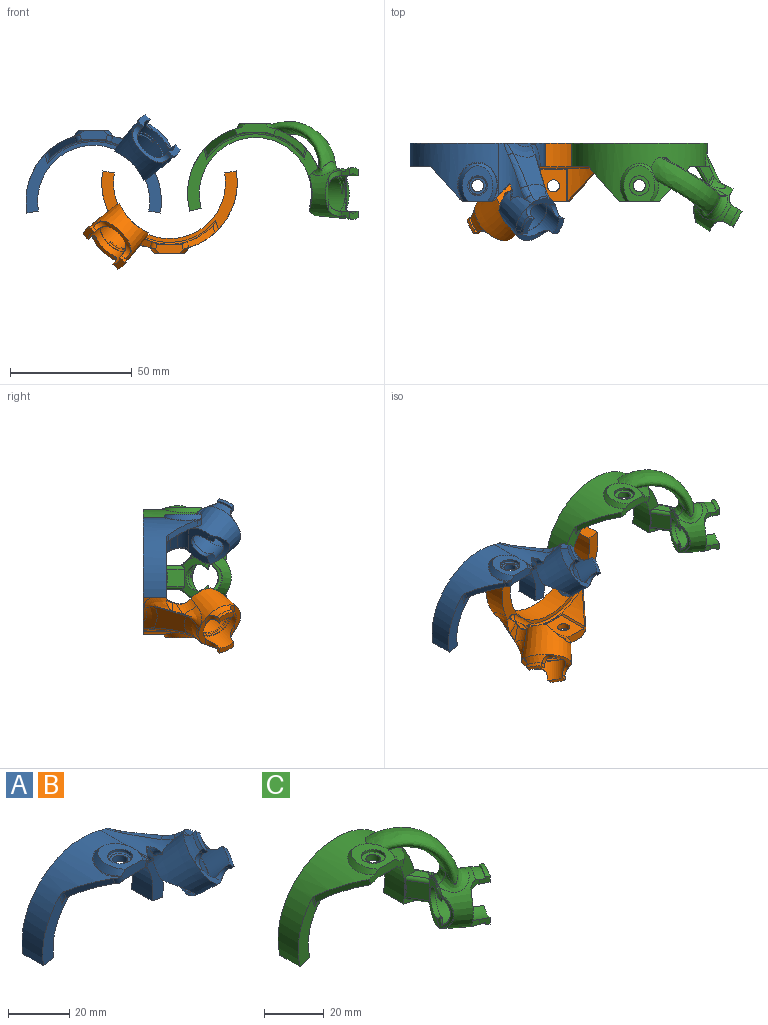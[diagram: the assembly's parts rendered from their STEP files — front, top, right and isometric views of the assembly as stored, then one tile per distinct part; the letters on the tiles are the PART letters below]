
ASSEMBLY  parts=3 mates=2
PART A: 82 faces, bbox 63.7x43.6x40.7 mm
  f0: cylinder r=27.82mm len=27.72mm, axis (0,-1,0), area 190.1mm2, adj f8,f10,f11,f62,f64
  f1: plane 11.92x10.64mm, normal (0.68,-0.71,-0.2), area 38.9mm2, adj f4,f5,f7,f27,f75,f76
  f2: cylinder r=2.48mm len=4.95mm, axis (0,0,-1), area 37.8mm2, adj f6,f21
  f3: cylinder r=2.54mm len=3.26mm, axis (-0.28,0,0.96), area 7.4mm2, adj f5,f7,f13,f14,f19,f21,f23,f25
  f4: cylinder r=2.54mm len=3.26mm, axis (-0.28,0,-0.96), area 7.4mm2, adj f1,f5,f7,f13,f19,f21,f24,f25
  f5: cylinder r=27.82mm len=36.56mm, axis (0,-1,0), area 638.5mm2, adj f1,f3,f4,f8,f10,f12,f14,f16
  f6: cylinder r=27.82mm len=7.09mm, axis (0,-1,0), area 19.5mm2, adj f2,f61
  f7: cylinder r=25.28mm len=35.25mm, axis (0,-1,0), area 190.1mm2, adj f1,f3,f4,f14,f15,f20,f22,f23
  f8: plane 55.71x29.42mm, normal (0,-1,0), area 248.8mm2, adj f0,f5,f9,f11,f12,f15,f16,f62
  f9: cylinder r=22.99mm len=45.98mm, axis (0,-1,0), area 764.4mm2, adj f8,f10,f11,f12
  f10: plane 56.02x33.04mm, normal (0,1,0), area 429.4mm2, adj f0,f5,f9,f11,f12,f63,f64,f77
  f11: plane 9.53x4.75mm, normal (-0.17,0,-0.98), area 46mm2, adj f0,f8,f9,f10
  f12: plane 9.53x4.75mm, normal (0.17,0,-0.98), area 46mm2, adj f5,f8,f9,f10
  f13: plane 11.35x3.84mm, normal (0,-1,0), area 39.1mm2, adj f3,f4,f18,f19,f21
  f14: plane 12.34x11.8mm, normal (-0.68,-0.71,-0.2), area 44.6mm2, adj f3,f5,f7,f15,f16
  f15: torus R=24.52mm, axis (0,-1,0), area 40.5mm2, adj f7,f8,f14,f16,f75
  f16: cylinder r=2.54mm len=5.13mm, axis (-0.28,0,0.96), area 6.7mm2, adj f5,f8,f14,f15
  f17: cylinder r=4.05mm len=8.1mm, axis (0,0,-1), area 24.8mm2, adj f18,f61
  f18: plane 14.63x12.64mm, normal (0,0,1), area 98.7mm2, adj f13,f17,f19
  f19: bspline ~16.86x15.94mm, area 92.9mm2, adj f3,f4,f13,f18,f25
  f20: plane 5.8x0.67mm, normal (0,-1,0), area 1.1mm2, adj f7,f21,f24
  f21: plane 12.98x10.54mm, normal (0,0,-1), area 117.5mm2, adj f2,f3,f4,f13,f20,f22,f23,f24
  f22: plane 5.8x0.67mm, normal (0,-1,0), area 1.1mm2, adj f7,f21,f23
  f23: plane 12.99x0.68mm, normal (0.78,0,-0.62), area 11.1mm2, adj f3,f7,f21,f22
  f24: plane 12.99x0.68mm, normal (-0.78,0,-0.62), area 11.1mm2, adj f4,f7,f20,f21
  f25: bspline ~17.23x16.47mm, area 14.5mm2, adj f3,f4,f5,f19
  f26: plane 4.77x4.77mm, normal (0.71,0,-0.71), area 13.3mm2, adj f55,f67,f70,f72
  f27: plane 11.43x9.08mm, normal (-0.65,-0.39,-0.65), area 33.3mm2, adj f1,f53,f56,f68,f69,f75
  f28: cone r=10.34mm half-angle=4.9deg, axis (0.59,-0.54,0.59), area 530.4mm2, adj f29,f30,f42,f43,f49,f52,f57,f58
  f29: cone r=10.34mm half-angle=8.1deg, axis (-0.59,0.54,-0.59), area 31.7mm2, adj f28,f32,f48,f51,f57,f58
  f30: cone r=10.34mm half-angle=8.1deg, axis (-0.59,0.54,-0.59), area 31.7mm2, adj f28,f31,f47,f50,f59,f60
  f31: plane 6.06x3.44mm, normal (-0.59,0.54,-0.59), area 6.6mm2, adj f30,f33,f47,f50
  f32: plane 6.06x3.44mm, normal (-0.59,0.54,-0.59), area 6.6mm2, adj f29,f34,f48,f51
  f33: cylinder r=10.72mm len=6.82mm, axis (-0.59,0.54,-0.59), area 10.3mm2, adj f31,f35,f47,f50
  f34: cylinder r=10.72mm len=6.82mm, axis (-0.59,0.54,-0.59), area 10.3mm2, adj f32,f36,f48,f51
  f35: plane 6.06x4.81mm, normal (0.59,-0.54,0.59), area 19.8mm2, adj f33,f37,f47,f50
  f36: plane 6.06x4.81mm, normal (0.59,-0.54,0.59), area 19.8mm2, adj f34,f37,f48,f51
  f37: cylinder r=8.05mm len=18.01mm, axis (-0.59,0.54,-0.59), area 249.8mm2, adj f35,f36,f40,f47,f48,f49,f50,f51
  f38: cylinder r=7.67mm len=17.35mm, axis (-0.59,0.54,-0.59), area 360.5mm2, adj f40,f41,f43,f44,f45,f46
  f39: cylinder r=5.29mm len=9.57mm, axis (-0.59,0.54,-0.59), area 42.1mm2, adj f41,f42,f43
  f40: plane 13.53x12.95mm, normal (0.59,-0.54,0.59), area 18.8mm2, adj f37,f38
  f41: plane 12.45x12.45mm, normal (0.59,-0.54,0.59), area 73.4mm2, adj f38,f39,f43
  f42: plane 15x15mm, normal (-0.59,0.54,-0.59), area 89mm2, adj f28,f39,f43,f67,f68,f69,f70
  f43: cylinder r=22.23mm len=11.7mm, axis (0,1,0), area 58.8mm2, adj f28,f38,f39,f41,f42
  f44: torus R=7.67mm, axis (-0.59,0.54,-0.59), area 23.4mm2, adj f38,f45,f46
  f45: plane 0.49x0.41mm, normal (0.71,0,-0.71), area 0.2mm2, adj f38,f44
  f46: plane 0.49x0.41mm, normal (0.71,0,-0.71), area 0.2mm2, adj f38,f44
  f47: plane 2.95x2.88mm, normal (-0.38,-0.84,-0.38), area 4.3mm2, adj f30,f31,f33,f35,f37,f59
  f48: plane 2.95x2.88mm, normal (-0.38,-0.84,-0.38), area 4.3mm2, adj f29,f32,f34,f36,f37,f58
  f49: plane 10.52x10.52mm, normal (0.59,-0.54,0.59), area 28.1mm2, adj f28,f37,f58,f59
  f50: plane 2.95x2.88mm, normal (0.38,0.84,0.38), area 4.3mm2, adj f30,f31,f33,f35,f37,f60
  f51: plane 2.95x2.88mm, normal (0.38,0.84,0.38), area 4.3mm2, adj f29,f32,f34,f36,f37,f57
  f52: plane 10.65x10.65mm, normal (0.59,-0.54,0.59), area 28.4mm2, adj f28,f37,f57,f60,f65,f81
  f53: plane 2.25x1.64mm, normal (-0.68,-0.28,-0.68), area 2.3mm2, adj f27,f63,f68,f76
  f54: plane 13.87x13.1mm, normal (0.65,0.39,0.65), area 138.7mm2, adj f55,f64,f65,f78
  f55: cylinder r=0.25mm len=15.15mm, axis (-0.27,0.92,-0.27), area 4.6mm2, adj f26,f54,f62,f66,f71
  f56: cylinder r=0.25mm len=3.04mm, axis (0.27,-0.92,0.27), area 0.6mm2, adj f27,f70,f74
  f57: cylinder r=3.56mm len=5.03mm, axis (0.71,0,-0.71), area 13.1mm2, adj f28,f29,f37,f51,f52
  f58: cylinder r=3.56mm len=7.36mm, axis (-0.71,0,0.71), area 13.1mm2, adj f28,f29,f37,f48,f49
  f59: cylinder r=3.56mm len=7.36mm, axis (-0.71,0,0.71), area 13.1mm2, adj f28,f30,f37,f47,f49
  f60: cylinder r=3.56mm len=5.03mm, axis (0.71,0,-0.71), area 13.1mm2, adj f28,f30,f37,f50,f52
  f61: bspline ~8.12x8.11mm, area 20.1mm2, adj f6,f17
  f62: bspline ~12.74x8.36mm, area 48.6mm2, adj f0,f8,f55,f64,f71,f72
  f63: cylinder r=10.92mm len=23.59mm, axis (0,-1,0), area 126.5mm2, adj f5,f10,f28,f53,f68,f76,f77,f78
  f64: bspline ~12.26x10.49mm, area 58.9mm2, adj f0,f10,f54,f62,f77
  f65: bspline ~11.42x11.17mm, area 64.6mm2, adj f28,f52,f54,f66,f79,f80,f81
  f66: bspline ~11.15x9.59mm, area 43.5mm2, adj f28,f55,f65,f67
  f67: bspline ~18.46x16.46mm, area 37mm2, adj f26,f28,f42,f66,f70
  f68: bspline ~12.69x12.02mm, area 17mm2, adj f27,f28,f42,f53,f63,f69
  f69: cylinder r=5.08mm len=8.78mm, axis (0.71,0,-0.71), area 48.6mm2, adj f27,f42,f68,f70
  f70: bspline ~7.07x5.36mm, area 3.7mm2, adj f26,f42,f56,f67,f69,f72,f73
  f71: bspline ~3.08x3.03mm, area 0mm2, adj f55,f62,f72
  f72: cylinder r=2.54mm len=5.65mm, axis (-0.71,0,-0.71), area 13.5mm2, adj f8,f26,f62,f70,f71,f73
  f73: bspline ~3.31x2.86mm, area 0.9mm2, adj f8,f70,f72,f74
  f74: bspline ~3.3x2.58mm, area 5.8mm2, adj f8,f56,f73,f75
  f75: cylinder r=2.54mm len=10.94mm, axis (-0.71,0,0.71), area 28.7mm2, adj f1,f7,f8,f15,f27,f74
  f76: bspline ~7.88x7.71mm, area 1.7mm2, adj f1,f5,f53,f63
  f77: bspline ~8.1x4.83mm, area 9.2mm2, adj f10,f63,f64,f78
  f78: bspline ~14.69x8.01mm, area 43.3mm2, adj f54,f63,f77,f79
  f79: bspline ~7.97x5.64mm, area 15.7mm2, adj f63,f65,f78,f80
  f80: bspline ~3.64x2.8mm, area 0.7mm2, adj f28,f65,f79,f81
  f81: bspline ~4.33x3.86mm, area 9.3mm2, adj f28,f52,f65,f80
PART B: same geometry as A
PART C: 123 faces, bbox 86.5x40.3x50.3 mm
  f0: cylinder r=7.8mm len=17.92mm, axis (-0.88,0.48,0), area 376mm2, adj f35,f47,f48,f49,f80,f81,f82,f91
  f1: plane 16.83x4.8mm, normal (0,-1,0), area 49.3mm2, adj f17,f19,f25,f26,f31,f32,f86,f87
  f2: cylinder r=2.48mm len=4.95mm, axis (0,0,-1), area 37.8mm2, adj f18,f86
  f3: cone r=10.21mm half-angle=4.9deg, axis (0.88,-0.48,0), area 394.1mm2, adj f6,f7,f9,f10,f41,f44,f50,f51
  f4: cylinder r=5.42mm len=10.83mm, axis (-0.88,0.48,0), area 45.1mm2, adj f36,f76,f79,f80,f82,f83,f91,f92
  f5: plane 8.22x7.83mm, normal (-0.86,-0.51,0), area 57.7mm2, adj f20,f36,f59,f61,f77
  f6: cone r=8.31mm half-angle=47.5deg, axis (0.88,-0.48,0), area 14.2mm2, adj f3,f36,f70,f76,f83,f84
  f7: cone r=8.31mm half-angle=47.5deg, axis (0.88,-0.48,0), area 2.5mm2, adj f3,f36,f71,f76,f78,f84
  f8: cylinder r=8.18mm len=18.31mm, axis (-0.88,0.48,0), area 166.1mm2, adj f15,f16,f35,f41,f42,f43,f44,f45
  f9: cone r=10.21mm half-angle=8.4deg, axis (-0.88,0.48,0), area 26.7mm2, adj f3,f12,f43,f46,f50,f51
  f10: cone r=10.21mm half-angle=8.4deg, axis (-0.88,0.48,0), area 26.7mm2, adj f3,f11,f42,f45,f52,f53
  f11: plane 6.54x3.61mm, normal (-0.88,0.48,0), area 6.8mm2, adj f10,f13,f42,f45
  f12: plane 6.54x3.61mm, normal (-0.88,0.48,0), area 6.8mm2, adj f9,f14,f43,f46
  f13: cylinder r=10.59mm len=7.3mm, axis (-0.88,0.48,0), area 12.1mm2, adj f11,f15,f42,f45
  f14: cylinder r=10.59mm len=7.3mm, axis (-0.88,0.48,0), area 12.1mm2, adj f12,f16,f43,f46
  f15: plane 6.54x3.61mm, normal (0.88,-0.48,0), area 18.5mm2, adj f8,f13,f42,f45
  f16: plane 6.54x3.61mm, normal (0.88,-0.48,0), area 18.5mm2, adj f8,f14,f43,f46
  f17: cylinder r=27.82mm len=55.64mm, axis (0,-1,0), area 1084.1mm2, adj f1,f20,f22,f23,f24,f25,f26,f28
  f18: cylinder r=27.82mm len=8.1mm, axis (0,-1,0), area 32.4mm2, adj f2,f30
  f19: cylinder r=25.28mm len=38.76mm, axis (0,-1,0), area 257.7mm2, adj f1,f25,f26,f27,f40,f85,f87,f88
  f20: plane 56.83x31.78mm, normal (0,-1,0), area 251.4mm2, adj f5,f17,f21,f23,f24,f27,f28,f29
  f21: cylinder r=22.99mm len=45.98mm, axis (0,-1,0), area 802.7mm2, adj f20,f22,f23,f24
  f22: plane 55.64x35.02mm, normal (0,1,0), area 449.4mm2, adj f17,f21,f23,f24
  f23: plane 9.53x4.66mm, normal (-0.26,0,-0.97), area 46mm2, adj f17,f20,f21,f22
  f24: plane 9.53x4.66mm, normal (0.26,0,-0.97), area 46mm2, adj f17,f20,f21,f22
  f25: plane 14.01x13.01mm, normal (0.68,-0.71,-0.2), area 53.3mm2, adj f1,f17,f19,f27,f28
  f26: plane 14.01x13.01mm, normal (-0.68,-0.71,-0.2), area 53.3mm2, adj f1,f17,f19,f27,f29
  f27: torus R=24.52mm, axis (0,-1,0), area 53.6mm2, adj f19,f20,f25,f26,f28,f29,f40,f90
  f28: cylinder r=1.02mm len=4.53mm, axis (0.28,0,0.96), area 2.9mm2, adj f17,f20,f25,f27
  f29: cylinder r=1.02mm len=4.53mm, axis (-0.28,0,0.96), area 2.9mm2, adj f17,f20,f26,f27
  f30: cylinder r=4.05mm len=8.1mm, axis (0,0,-1), area 30.2mm2, adj f18,f31
  f31: plane 16.69x14.85mm, normal (0,0,1), area 102.5mm2, adj f1,f30,f32
  f32: bspline ~16.48x15.78mm, area 58.7mm2, adj f1,f17,f31,f38
  f33: plane 6.25x6.23mm, normal (0,0,-1), area 19.8mm2, adj f20,f60,f61,f66,f70
  f34: plane 6.25x6.23mm, normal (0,0,1), area 19.8mm2, adj f20,f58,f59,f62,f75
  f35: plane 16.36x14.32mm, normal (0.88,-0.48,0), area 19.1mm2, adj f0,f8
  f36: plane 17.15x10.58mm, normal (-0.88,0.48,0), area 71.8mm2, adj f4,f5,f6,f7,f59,f61,f70,f71
  f37: plane 10.24x6.99mm, normal (0.9,0.43,0), area 74.1mm2, adj f58,f60,f64,f68
  f38: bspline ~33.42x32.82mm, area 654.6mm2, adj f17,f32,f54,f56,f94,f98
  f39: plane 22.53x17.34mm, normal (0.48,0.87,-0.14), area 75.6mm2, adj f57,f94,f95,f96,f98,f99,f101
  f40: bspline ~28.97x28.69mm, area 0.2mm2, adj f19,f27,f90
  f41: plane 13.09x2.14mm, normal (0.88,-0.48,0), area 19.2mm2, adj f3,f8,f51,f52
  f42: plane 3.34x2.64mm, normal (-0.48,-0.88,0), area 8.3mm2, adj f8,f10,f11,f13,f15,f52
  f43: plane 3.34x2.64mm, normal (-0.48,-0.88,0), area 8.3mm2, adj f8,f9,f12,f14,f16,f51
  f44: plane 13.09x2.14mm, normal (0.88,-0.48,0), area 19.2mm2, adj f3,f8,f50,f53
  f45: plane 3.34x2.64mm, normal (0.48,0.88,0), area 8.3mm2, adj f8,f10,f11,f13,f15,f53
  f46: plane 3.34x2.64mm, normal (0.48,0.88,0), area 8.3mm2, adj f8,f9,f12,f14,f16,f50
  f47: torus R=7.8mm, axis (-0.88,0.48,0), area 25.7mm2, adj f0,f48,f49
  f48: plane 0.64x0.51mm, normal (0,0,-1), area 0.2mm2, adj f0,f47
  f49: plane 0.64x0.51mm, normal (0,0,-1), area 0.2mm2, adj f0,f47
  f50: cylinder r=3.81mm len=6.26mm, axis (0,0,-1), area 12.6mm2, adj f3,f8,f9,f44,f46
  f51: cylinder r=3.81mm len=6.26mm, axis (0,0,1), area 12.6mm2, adj f3,f8,f9,f41,f43
  f52: cylinder r=3.81mm len=6.26mm, axis (0,0,1), area 12.6mm2, adj f3,f8,f10,f41,f42
  f53: cylinder r=3.81mm len=6.26mm, axis (0,0,-1), area 12.6mm2, adj f3,f8,f10,f44,f45
  f54: bspline ~7.44x6.47mm, area 34.7mm2, adj f38,f55,f56,f72,f95
  f55: bspline ~7.43x6.95mm, area 7.8mm2, adj f3,f54,f73,f96,f97
  f56: bspline ~13.81x13.06mm, area 87.8mm2, adj f3,f38,f54,f71,f99,f100
  f57: bspline ~38.57x21.21mm, area 21.3mm2, adj f3,f39,f97,f100
  f58: cylinder r=1.27mm len=11.61mm, axis (0.43,-0.9,0), area 19.4mm2, adj f20,f34,f37,f63,f67
  f59: cylinder r=1.27mm len=8.02mm, axis (-0.51,0.86,0), area 15.9mm2, adj f5,f20,f34,f36,f75
  f60: cylinder r=1.27mm len=11.61mm, axis (-0.43,0.9,0), area 19.4mm2, adj f20,f33,f37,f65,f69
  f61: cylinder r=1.27mm len=8.02mm, axis (0.51,-0.86,0), area 15.9mm2, adj f5,f20,f33,f36,f70
  f62: bspline ~22.47x12.27mm, area 3.9mm2, adj f3,f34,f63,f75
  f63: bspline ~7.53x5.56mm, area 20.4mm2, adj f3,f58,f62,f64
  f64: bspline ~6.99x2.91mm, area 21.5mm2, adj f3,f37,f63,f65
  f65: bspline ~6.49x5.05mm, area 20.4mm2, adj f3,f60,f64,f66
  f66: bspline ~35.46x17.86mm, area 3.9mm2, adj f3,f33,f65,f70
  f67: bspline ~6.82x3.97mm, area 11.6mm2, adj f17,f20,f58,f68
  f68: bspline ~6.99x1.52mm, area 7.7mm2, adj f17,f37,f67,f69
  f69: bspline ~6.7x3.58mm, area 11.6mm2, adj f17,f20,f60,f68
  f70: bspline ~3.98x2.92mm, area 2.8mm2, adj f6,f33,f36,f61,f66
  f71: bspline ~1.71x1.24mm, area 1.4mm2, adj f7,f36,f56,f72
  f72: bspline ~5.42x3.41mm, area 5.3mm2, adj f36,f54,f71,f73
  f73: bspline ~1.41x1.39mm, area 1.3mm2, adj f36,f55,f72,f74
  f74: cone r=8.31mm half-angle=47.5deg, axis (0.88,-0.48,0), area 2.1mm2, adj f3,f36,f73,f75
  f75: bspline ~3.98x2.91mm, area 2.8mm2, adj f34,f36,f59,f62,f74
  f76: cylinder r=23.24mm len=13.92mm, axis (0,1,0), area 26.7mm2, adj f4,f6,f7,f78,f79,f80,f81,f82
  f77: cylinder r=23.24mm len=6.79mm, axis (0,1,0), area 0mm2, adj f5,f20
  f78: bspline ~2.53x1.27mm, area 0.4mm2, adj f7,f36,f76,f79
  f79: bspline ~3.94x2.76mm, area 0.9mm2, adj f4,f36,f76,f78,f80
  f80: bspline ~2.83x1.25mm, area 1.7mm2, adj f0,f4,f76,f79,f81,f93
  f81: bspline ~12.52x4.28mm, area 6.9mm2, adj f0,f76,f80,f82
  f82: bspline ~2.87x1.26mm, area 1.8mm2, adj f0,f4,f76,f81,f92
  f83: bspline ~2.7x1.33mm, area 0.4mm2, adj f4,f6,f36,f76
  f84: bspline ~15.01x5.63mm, area 5.4mm2, adj f3,f6,f7,f76
  f85: plane 5.08x0.52mm, normal (0,-1,0), area 0.9mm2, adj f19,f86,f88
  f86: plane 13.28x10.16mm, normal (0,0,-1), area 115.7mm2, adj f1,f2,f85,f87,f88,f89
  f87: plane 13.28x0.52mm, normal (1,0,0), area 6.9mm2, adj f1,f19,f86,f89
  f88: plane 13.28x0.52mm, normal (-1,0,0), area 6.9mm2, adj f1,f19,f85,f86
  f89: plane 5.08x0.52mm, normal (0,-1,0), area 0.9mm2, adj f19,f86,f87
  f90: bspline ~4.75x3.92mm, area 4.4mm2, adj f19,f27,f40
  f91: plane 15.6x9.75mm, normal (0.88,-0.48,0), area 63.3mm2, adj f0,f4,f92,f93
  f92: bspline ~3.62x2.56mm, area 5.7mm2, adj f0,f4,f82,f91
  f93: bspline ~3.62x2.56mm, area 5.7mm2, adj f0,f4,f80,f91
  f94: bspline ~20.39x13.51mm, area 24.5mm2, adj f17,f38,f39,f95,f101
  f95: bspline ~0.93x0.28mm, area 0.1mm2, adj f39,f54,f94,f96
  f96: bspline ~2.23x1.03mm, area 1.7mm2, adj f39,f55,f95,f97
  f97: bspline ~3.8x2.12mm, area 1.2mm2, adj f55,f57,f96
  f98: bspline ~26.24x17.22mm, area 34.1mm2, adj f17,f38,f39,f99,f101
  f99: bspline ~1.12x0.94mm, area 0.7mm2, adj f39,f56,f98,f100
  f100: bspline ~3.51x3.41mm, area 1.5mm2, adj f56,f57,f99
  f101: bspline ~3.41x2.76mm, area 3mm2, adj f17,f39,f94,f98
  f102: plane 2.23x1.23mm, normal (-0.26,0,0.97), area 2.8mm2, adj f103,f104,f105,f106
  f103: cylinder r=26.04mm len=52.08mm, axis (0,-1,0), area 207.4mm2, adj f102,f104,f106,f107
  f104: plane 52.08x31.55mm, normal (0,1,0), area 115mm2, adj f102,f103,f105,f107
  f105: cylinder r=24.77mm len=49.54mm, axis (0,-1,0), area 197mm2, adj f102,f104,f106,f107
  f106: plane 52.08x31.55mm, normal (0,-1,0), area 115mm2, adj f102,f103,f105,f107
  f107: plane 2.23x1.23mm, normal (0.26,0,0.97), area 2.8mm2, adj f103,f104,f105,f106
  f108: plane 2.24x1.55mm, normal (0.48,0.87,-0.14), area 1.6mm2, adj f109,f113,f114
  f109: cylinder r=26.04mm len=51.64mm, axis (0,-1,0), area 218.7mm2, adj f108,f111,f112,f113,f114,f115,f116,f121
  f110: plane 9.53x1.65mm, normal (-0.89,0.45,0), area 11.1mm2, adj f111,f117,f120,f121
  f111: plane 2.72x1.29mm, normal (0,0,1), area 2.8mm2, adj f109,f110,f112,f120,f121
  f112: plane 18.95x16.46mm, normal (0,1,0), area 31.5mm2, adj f109,f111,f113,f120
  f113: bspline ~2.36x2.28mm, area 2.3mm2, adj f108,f109,f112,f114,f120
  f114: plane 2.42x2.21mm, normal (-0.76,0.33,-0.56), area 4.7mm2, adj f108,f109,f113,f115,f120
  f115: plane 34.55x31.55mm, normal (0,1,0), area 67.7mm2, adj f109,f114,f116,f120
  f116: plane 2.72x1.23mm, normal (-0.26,0,0.97), area 3.5mm2, adj f109,f115,f120,f121
  f117: plane 2.72x1.29mm, normal (0,0,-1), area 2.8mm2, adj f110,f118,f119,f120,f121
  f118: cylinder r=26.04mm len=2.72mm, axis (0,-1,0), area 2.1mm2, adj f117,f119,f121,f122
  f119: plane 1.38x0.74mm, normal (0,1,0), area 0.7mm2, adj f117,f118,f120,f122
  f120: cylinder r=24.77mm len=49.54mm, axis (0,-1,0), area 223.3mm2, adj f110,f111,f112,f113,f114,f115,f116,f117
  f121: plane 51.64x31.55mm, normal (0,-1,0), area 107.9mm2, adj f109,f110,f111,f116,f117,f118,f120,f122
  f122: plane 2.72x1.23mm, normal (0.26,0,0.97), area 3.5mm2, adj f118,f119,f120,f121
PLACE A t=(26.97,10.41,-9.14)mm
PLACE B rot(axis=(0,1,0),180deg) t=(58.1,10.41,-1.49)mm
PLACE C t=(93.34,10.41,-5.96)mm
MATE planar C.f22 <-> B.f10  axis (0,1,0) through (71.13,19.93,-11.91)mm
MATE planar A.f10 <-> B.f10  axis (0,1,0) through (27.01,19.93,5.27)mm
